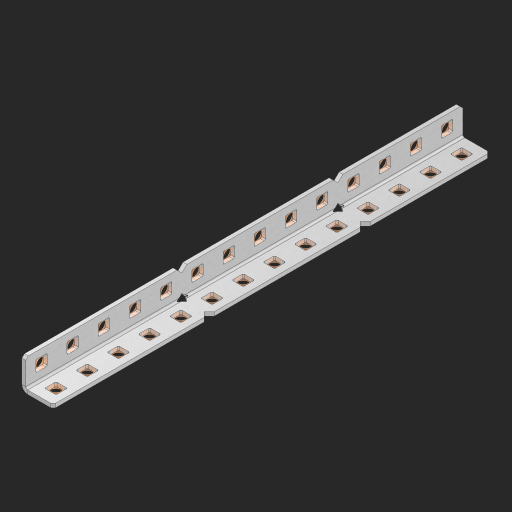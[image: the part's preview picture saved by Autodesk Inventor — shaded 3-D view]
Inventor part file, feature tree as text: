
AUTODESK INVENTOR PART (.ipt)
format: ipt  version: 2023 (Build 270158000, 158)  size: 676,864 bytes
history: native  units: in
note: dims shown in document units (in); Inventor stores cm internally (conversion verified against a paired STEP export)
features: other x34, extrude x29, sheet_metal_op x8, sketch x5, pattern_linear x1, mirror x1, chamfer x1
ambient origin geometry x8: Origin, YZ Plane, XZ Plane, XY Plane, X Axis, Y Axis, Z Axis, Center Point
bodies: Solid1 (feature_tree), Body (feature_tree)
feature tree (79):
  sheet_metal_op  "Flanges"
  sheet_metal_op  "Body Pattern"
  other  "Arc Length"
  pattern_linear  "Notch Pattern"  Spacing1=0.125in  [1 undecoded]
  other  "Diagonal Plane"
  mirror  "Everything Mirrored"
  chamfer  "End Chamfer"
  sketch  "Sketch1"  dims[d0=0.5in]
  other  "Plate1"
  sketch  "Sketch2"  dims[d1=7.0in]
  other  "Plate2"
  sheet_metal_op  "Bend1"
  sheet_metal_op  "Corner1"
  sketch  "Sketch8"  dims[d2=0.0625in]
  sketch  "Sketch9"  dims[d3=0.0625in]
  other  "Srf91"
  sheet_metal_op  "Body Pattern Sketch"
  other  "Srf92"
  sketch  "Sketch13"  dims[d4=0.0312in d5=0.125in d6=0.0625in d7=0.5in d8=90.0deg d9=0.0312in d10=0.25in d11=0.0625in d12=0.0625in d49=0.182in d50=0.02in d52=0.25in d53=0.0625in d54=0.0in d55=0.172in d56=1.0in d57=0.0in d85=0.1473in d86=0.1782in d89=0.0625in d90=0.0in d91=0.04in d92=0.0491in d95=2.5in d96=0.04in d97=0.25in d98=45.0deg d123=0.204in d126=0.0491in d127=0.1473in d128=0.08in d129=0.04in d130=2.5in d131=5.5118in d133=0.5in d134=0.3937in d136=1.0in]
  other  "Srf856"
  other  "Srf857"
  other  "Srf858"
  other  "Srf859"
  other  "Srf860"
  other  "Srf861"
  other  "Srf1275"
  other  "Srf1276"
  other  "Srf1278"
  other  "Srf1279"
  other  "Srf1280"
  other  "Srf1281"
  other  "Srf1282"
  other  "Srf1283"
  other  "Srf1383"
  other  "Srf1384"
  other  "Srf1385"
  other  "Srf1386"
  other  "Srf1387"
  other  "Srf1388"
  other  "Srf1389"
  other  "Srf1475"
  other  "Srf1476"
  other  "Srf1477"
  other  "Srf1478"
  other  "Srf1479"
  other  "Srf1480"
  other  "Srf1481"
  sheet_metal_op  "Body Stamp"
  sheet_metal_op  "Body Circle"
  sheet_metal_op  "Notch"
  extrude  "ExtrusionSrf92"  Depth=0.0625in
  extrude  "ExtrusionSrf856"  Depth=0.5in TaperAngle=90.0deg
  extrude  "ExtrusionSrf857"  Depth=0.25in
  extrude  "ExtrusionSrf858"  Depth=0.0625in
  extrude  "ExtrusionSrf859"  Depth=0.0625in
  extrude  "ExtrusionSrf860"  Depth=0.3937in
  extrude  "ExtrusionSrf861"  Depth=0.02in
  extrude  "ExtrusionSrf1275"  Depth=0.25in
  extrude  "ExtrusionSrf1276"  Depth=0.0625in
  extrude  "ExtrusionSrf1277"  TaperAngle=0.0deg  [1 undecoded]
  extrude  "ExtrusionSrf1278"  Depth=0.3937in
  extrude  "ExtrusionSrf1279"  Depth=0.3937in TaperAngle=0.0deg
  extrude  "ExtrusionSrf1280"  Depth=0.3937in
  extrude  "ExtrusionSrf1281"  Depth=0.3937in
  extrude  "ExtrusionSrf1282"  Depth=0.0625in
  extrude  "ExtrusionSrf1383"  Depth=0.3937in TaperAngle=0.0deg
  extrude  "ExtrusionSrf1384"  Depth=0.3937in
  extrude  "ExtrusionSrf1385"  Depth=0.25in TaperAngle=45.0deg
  extrude  "ExtrusionSrf1386"  Depth=0.3937in
  extrude  "ExtrusionSrf1387"  Depth=0.3937in
  extrude  "ExtrusionSrf1388"  Depth=0.3937in
  extrude  "ExtrusionSrf1389"  Depth=0.3937in
  extrude  "ExtrusionSrf1475"  Depth=0.3937in
  extrude  "ExtrusionSrf1476"  Depth=0.3937in
  extrude  "ExtrusionSrf1477"  Depth=0.3937in
  extrude  "ExtrusionSrf1478"  Depth=0.5in
  extrude  "ExtrusionSrf1479"  [1 undecoded]
  extrude  "ExtrusionSrf1480"  [1 undecoded]
  extrude  "ExtrusionSrf1481"  [1 undecoded]
note: 5 required parameter values undecoded (feature->parameter linkage not recoverable at this tier; creation-order binding heuristic only, values carry confidence <= 0.55)
